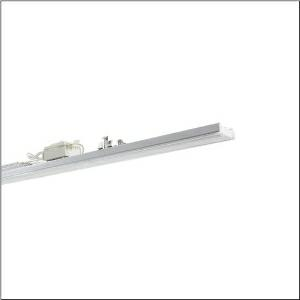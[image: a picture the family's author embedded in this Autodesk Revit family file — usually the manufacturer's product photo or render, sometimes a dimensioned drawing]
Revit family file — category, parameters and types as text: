
# Revit family: licross_r__21_recessed_ho_52tl1edn4axs_2080
name_source: partatom
category: Lighting Fixtures
units: mm (PartAtom-declared; Revit-internal decimal feet)

## family parameters
Cut with Voids When Loaded = No
Host = Face
Light Source = No
Part Type = Normal
Room Calculation Point = No
Round Connector Dimension = Use Diameter
Shared = No

## types (1)
- --- (1 x LED, 10000 lm, 56.1 W, 4000K)
    Apparent Load = 56 VA
    CIE Flux Codes = 85 95 99 100 100
    Color Rendering = 80
    Color Temperature = 4000K
    Default Elevation = 1800 mm
    Description = Licross® 21 Recessed HO, luminaire insert, of sheet steel, galvanised, coil coated, white, length: 1.500mm, width: 66mm, height: 67mm, LED rated luminous flux: 10.000lm, light colour: 840, control gear: DALI 2, with plug, 5-pole, with phase selection, mains connection: 220..240V, AC, 50/60Hz, rated input power: 56W, halogen-free wiring, primary light control with lens, of plastic, primary optical cover: cover, of PMMA, light emission: direct distribution, primary light characteristic: symmetric, protection rating (complete): IP40, insulation class (complete): insulation class I (protective earthing), certification: CE, ENEC, VDE, UKCA, protection symbol: D if used in an environment without relevant dust loads with corresponding accessories, impact resistance: IK06, permissible ambient temperature for indoor applications: -25..+40°C, corresponds to IFS (International Featured Standards) requirements for safety and quality in the food industry, reducing of maximum allowable ambient temperature of 5°C with ceiling mounting, LABS conformity tested according to VDMA 24364:2018-05, packaging unit: 1 piece
    Height = 58 mm
    Lamp = 1 x LED
    Lamp Light Flux = 10000 lm
    Lamp Power = 56.1 W
    Lamp count = 1
    Length = 1500 mm
    Luminous efficacy = 178 lm/W
    Manufacturer = Siteco
    ModVariant = No
    Model = 52TL1EDN4AXS
    Mounting Place = Ceiling
    Mounting Type = Pendant
    Number of Poles = 1
    OnlyDefault = Yes
    Power Factor = 1
    Product Name = Licross® 21 Recessed HO
    Product group = luminaire insert
    ProductGroupID = 902
    Protection Class = Protection class I
    Protection Degree = IP 40
    RLX_Detail_Level = 1
    RLX_Emergency_Light_Flux = 0 lm
    RLX_Emergency_Type = 0
    RLX_Emergency_Type_DB = No
    RlxData = <blob elided: 24429 chars, md5=c988445b>
    Socket = socket
    Standby Power = 0 W
    System Light Flux = 10000 lm
    System Power = 56 W
    Type Comments = factory setting: luminous flux: 100 % | dim-lin: 254 | 321 mA
    Type Image = l_1296930.jpg
    URL = http://relux.com
    VarID = @adj_125138
    Voltage = 0 V
    Weight = 0.00 kg
    Width = 66 mm

## geometry (parser evidence)
native form markers: Blend x4, Sweep x11
no freeform markers — native parametric forms only
